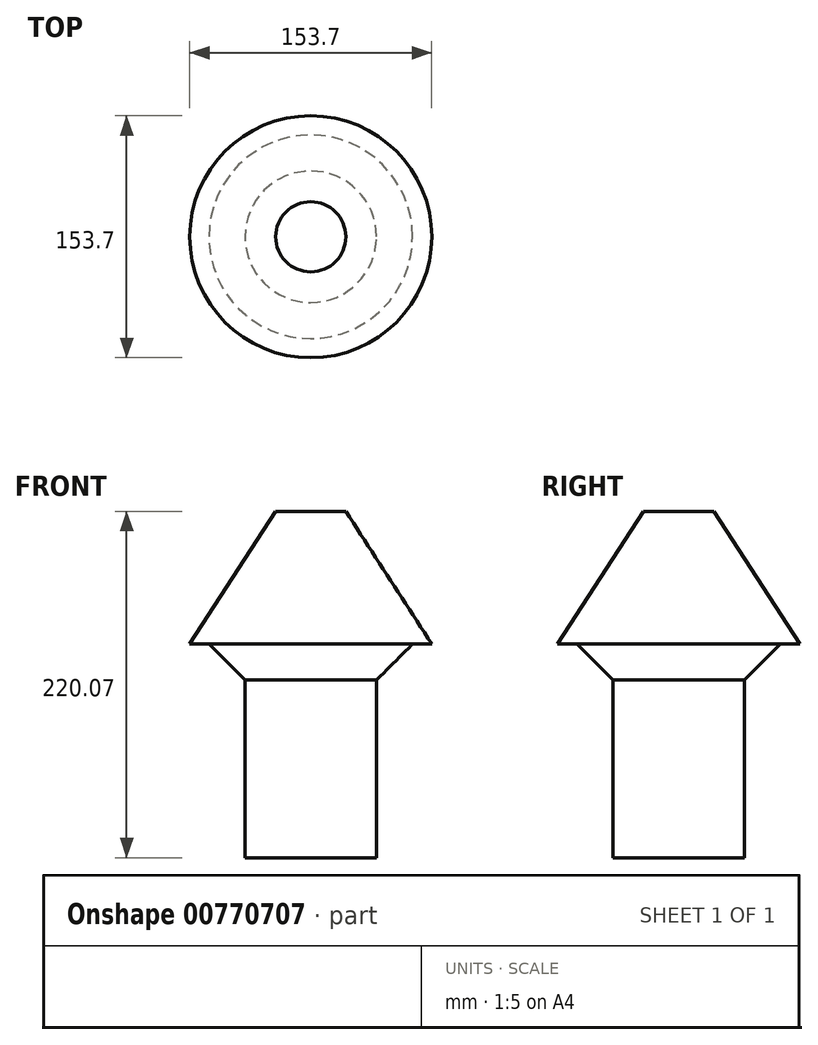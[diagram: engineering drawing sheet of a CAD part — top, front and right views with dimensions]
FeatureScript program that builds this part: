
annotation { "Feature Type Name" : "Feature", "Feature Type Description" : "" }
export const myFeature = defineFeature(function(context is Context, id is Id, definition is map)
    precondition{}
    {
        {
            var Q0;
            Q0=qCreatedBy(makeId("Front.planeOp"),FACE);
            var sketch = newSketch(context, id + "F0", { "sketchPlane" : qUnion([Q0])});
            skLineSegment(sketch, "E0", {"start": v(41.77, 0) * mm, "end": v(0, 0) * mm});
            skLineSegment(sketch, "E1", {"start": v(41.77, 135.71) * mm, "end": v(41.77, 0) * mm});
            skLineSegment(sketch, "E2", {"start": v(41.77, 135.71) * mm, "end": v(76.85, 135.71) * mm});
            skLineSegment(sketch, "E3", {"start": v(76.85, 135.71) * mm, "end": v(22.27, 220.07) * mm});
            skLineSegment(sketch, "E4", {"start": v(22.27, 220.07) * mm, "end": v(0, 220.07) * mm});
            skLineSegment(sketch, "E5", {"start": v(0, 220.07) * mm, "end": v(0, 0) * mm});
            skSolve(sketch);
        }
        {
            var Q0;
            Q0=makeQuery(id+"F0.imprint","IMPRINT",FACE,{"disambiguationData":[TD([[makeQuery(id+"F0.imprint","IMPRINT",EDGE,{"derivedFrom":sQuery(id+"F0.wireOp",EDGE,"E0")}),-1.0]])]});
            var Q1;
            Q1=sQuery(id+"F0.wireOp",EDGE,"E5");
            revolve(context, id + "F1", {"surfaceOperationType" : NewSurfaceOperationType.NEW, "entities" : qUnion([Q0]), "axis" : qUnion([Q1]), "revolveType" : RevolveType.FULL});
        }
        {
            var Q0;
            Q0=makeQuery(id+"F1.opRevolve","SWEPT_EDGE",EDGE,{"disambiguationData":[OSD([sQuery(id+"F0.wireOp",EDGE,"E1"),sQuery(id+"F0.wireOp",EDGE,"E2")])]});
            chamfer(context, id + "F2", {"entities" : qUnion([Q0]), "width" : 22.86 * mm, "tangentPropagation" : true});
        }
    });
